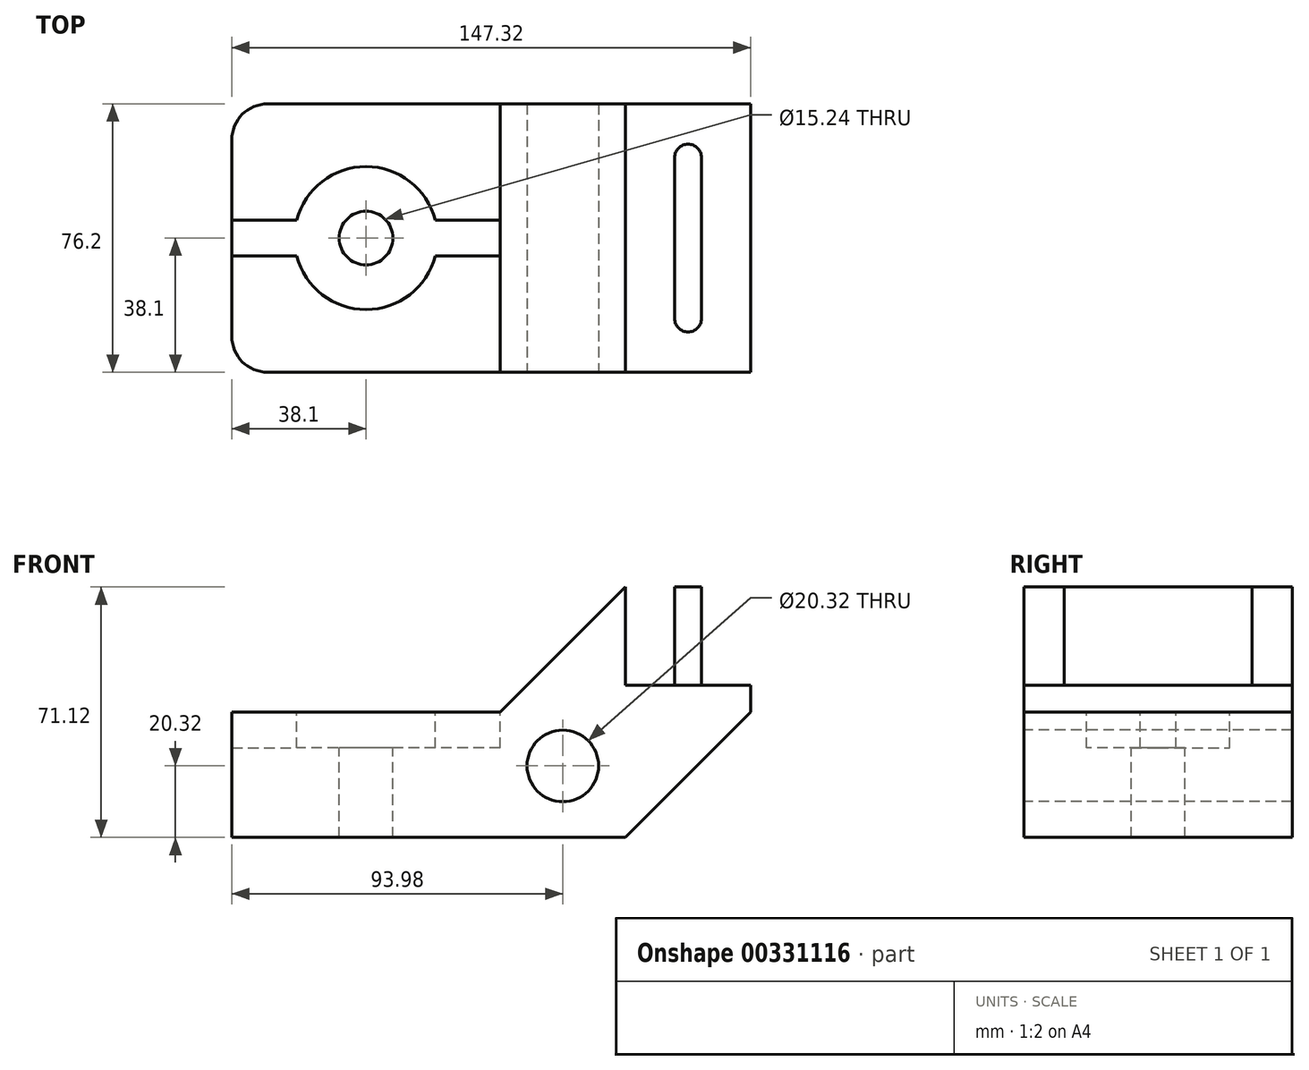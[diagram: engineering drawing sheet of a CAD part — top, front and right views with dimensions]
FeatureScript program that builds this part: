
annotation { "Feature Type Name" : "Feature", "Feature Type Description" : "" }
export const myFeature = defineFeature(function(context is Context, id is Id, definition is map)
    precondition{}
    {
        {
            var Q0;
            Q0=qCreatedBy(makeId("Front.planeOp"),FACE);
            var sketch = newSketch(context, id + "F0", { "sketchPlane" : qUnion([Q0])});
            skLineSegment(sketch, "E0", {"start": v(0, 0) * mm, "end": v(0, 35.56) * mm});
            skLineSegment(sketch, "E1", {"start": v(0, 35.56) * mm, "end": v(76.2, 35.56) * mm});
            skLineSegment(sketch, "E2", {"start": v(76.2, 35.56) * mm, "end": v(111.76, 71.12) * mm});
            skLineSegment(sketch, "E3", {"start": v(111.76, 71.12) * mm, "end": v(147.32, 71.12) * mm});
            skLineSegment(sketch, "E4", {"start": v(147.32, 71.12) * mm, "end": v(147.32, 35.56) * mm});
            skLineSegment(sketch, "E5", {"start": v(147.32, 35.56) * mm, "end": v(111.76, 0) * mm});
            skLineSegment(sketch, "E6", {"start": v(111.76, 0) * mm, "end": v(0, 0) * mm});
            skSolve(sketch);
        }
        {
            var Q0;
            Q0=makeQuery(id+"F0.imprint","IMPRINT",FACE,{"disambiguationData":[TD([[makeQuery(id+"F0.imprint","IMPRINT",EDGE,{"derivedFrom":sQuery(id+"F0.wireOp",EDGE,"E0")}),-1.0]])]});
            extrude(context, id + "F1", {"entities" : qUnion([Q0]), "oppositeDirection" : true, "depth" : 76.2 * mm});
        }
        {
            var Q0;
            Q0=makeQuery(id+"F1.opExtrude","SWEPT_FACE",FACE,{"disambiguationData":[OSD([sQuery(id+"F0.wireOp",EDGE,"E3")])]});
            var sketch = newSketch(context, id + "F2", { "sketchPlane" : qUnion([Q0])});
            skLineSegment(sketch, "E7", {"start": v(129.54, 60.96) * mm, "end": v(129.54, 15.24) * mm, "construction": true});
            skArc(sketch, "E8.0.startCap", {"start": v(125.73, 60.96) * mm, "mid": v(129.54, 64.77) * mm, "end": v(133.35, 60.96) * mm});
            skArc(sketch, "E8.0.endCap", {"start": v(133.35, 15.24) * mm, "mid": v(129.54, 11.43) * mm, "end": v(125.73, 15.24) * mm});
            skLineSegment(sketch, "E8.0.left", {"start": v(133.35, 60.96) * mm, "end": v(133.35, 15.24) * mm});
            skLineSegment(sketch, "E8.0.right", {"start": v(125.73, 60.96) * mm, "end": v(125.73, 15.24) * mm});
            skSolve(sketch);
        }
        {
            var Q0;
            Q0=makeQuery(id+"F2.imprint","IMPRINT",FACE,{"disambiguationData":[TD([[makeQuery(id+"F2.imprint","IMPRINT",EDGE,{"derivedFrom":sQuery(id+"F2.wireOp",EDGE,"E8.0.startCap")}),-1.0]])]});
            extrude(context, id + "F3", {"entities" : qUnion([Q0]), "operationType" : NewBodyOperationType.REMOVE, "oppositeDirection" : true, "depth" : 27.94 * mm});
        }
        {
            var Q0;
            Q0=makeQuery(id+"F1.opExtrude","SWEPT_FACE",FACE,{"disambiguationData":[OSD([sQuery(id+"F0.wireOp",EDGE,"E1")])]});
            var sketch = newSketch(context, id + "F4", { "sketchPlane" : qUnion([Q0])});
            skLineSegment(sketch, "E9", {"start": v(0, 43.18) * mm, "end": v(19.74, 43.18) * mm});
            skLineSegment(sketch, "E10", {"start": v(56.46, 43.18) * mm, "end": v(76.2, 43.18) * mm});
            skLineSegment(sketch, "E11", {"start": v(76.2, 43.18) * mm, "end": v(76.2, 33.02) * mm});
            skLineSegment(sketch, "E12", {"start": v(76.2, 33.02) * mm, "end": v(56.46, 33.02) * mm});
            skLineSegment(sketch, "E13", {"start": v(19.74, 33.02) * mm, "end": v(0, 33.02) * mm});
            skLineSegment(sketch, "E14", {"start": v(0, 33.02) * mm, "end": v(0, 43.18) * mm});
            skCircle(sketch, "E15", {"center": v(38.1, 38.1) * mm, "radius": 19.05 * mm});
            skSolve(sketch);
        }
        {
            var Q0;
            Q0=sQuery(id+"F4.wireOp",VERTEX,"E15.center");
            var Q1;
            Q1=makeQuery(id+"F1.opExtrude","SWEPT_BODY",BODY,{"disambiguationData":[OSD([sQuery(id+"F0.wireOp",EDGE,"E0"),sQuery(id+"F0.wireOp",EDGE,"E1"),sQuery(id+"F0.wireOp",EDGE,"E2"),sQuery(id+"F0.wireOp",EDGE,"E3"),sQuery(id+"F0.wireOp",EDGE,"E4"),sQuery(id+"F0.wireOp",EDGE,"E5"),sQuery(id+"F0.wireOp",EDGE,"E6")])]});
            hole(context, id + "F5", {"style" : HoleStyle.C_BORE, "endStyle" : HoleEndStyle.THROUGH, "holeDiameter" : 15.24 * mm, "cBoreDiameter" : 40.64 * mm, "cBoreDepth" : 10.16 * mm, "tappedDepth" : 12.7 * mm, "tapClearance" : 3, "locations" : qUnion([Q0]), "scope" : qUnion([Q1])});
        }
        {
            var Q0;
            {var subQ0=sQuery(id+"F4.wireOp",EDGE,"E9");Q0=makeQuery(id+"F4.imprint","IMPRINT",FACE,{"disambiguationData":[TD([[makeQuery(id+"F4.imprint","IMPRINT",EDGE,{"derivedFrom":subQ0}),-1.0]])]});}
            var Q1;
            {var subQ0=sQuery(id+"F4.wireOp",EDGE,"E10");Q1=makeQuery(id+"F4.imprint","IMPRINT",FACE,{"disambiguationData":[TD([[makeQuery(id+"F4.imprint","IMPRINT",EDGE,{"derivedFrom":subQ0}),-1.0]])]});}
            extrude(context, id + "F6", {"entities" : qUnion([Q0, Q1]), "operationType" : NewBodyOperationType.REMOVE, "oppositeDirection" : true, "depth" : 10.16 * mm});
        }
        {
            var Q0;
            Q0=makeQuery(id+"F1.opExtrude","CAP_FACE",FACE,{"disambiguationData":[OSD([sQuery(id+"F0.wireOp",EDGE,"E0"),sQuery(id+"F0.wireOp",EDGE,"E1"),sQuery(id+"F0.wireOp",EDGE,"E2"),sQuery(id+"F0.wireOp",EDGE,"E3"),sQuery(id+"F0.wireOp",EDGE,"E4"),sQuery(id+"F0.wireOp",EDGE,"E5"),sQuery(id+"F0.wireOp",EDGE,"E6")])],"isStart":true});
            var sketch = newSketch(context, id + "F7", { "sketchPlane" : qUnion([Q0])});
            skCircle(sketch, "E16", {"center": v(93.98, 20.32) * mm, "radius": 10.16 * mm});
            skSolve(sketch);
        }
        {
            var Q0;
            Q0=makeQuery(id+"F7.imprint","IMPRINT",FACE,{"disambiguationData":[TD([[makeQuery(id+"F7.imprint","IMPRINT",EDGE,{"derivedFrom":sQuery(id+"F7.wireOp",EDGE,"E16")}),1.0]])]});
            extrude(context, id + "F8", {"entities" : qUnion([Q0]), "operationType" : NewBodyOperationType.REMOVE, "endBound" : BoundingType.THROUGH_ALL, "oppositeDirection" : true, "depth" : 25.4 * mm});
        }
        {
            var Q0;
            Q0=makeQuery(id+"F1.opExtrude","CAP_EDGE",EDGE,{"disambiguationData":[OSD([sQuery(id+"F0.wireOp",EDGE,"E0")])],"isStart":true});
            var Q1;
            Q1=makeQuery(id+"F1.opExtrude","CAP_EDGE",EDGE,{"disambiguationData":[OSD([sQuery(id+"F0.wireOp",EDGE,"E0")])],"isStart":false});
            fillet(context, id + "F9", {"entities" : qUnion([Q0, Q1]), "radius" : 10.16 * mm, "tangentPropagation" : true, "allowEdgeOverflow" : false});
        }
    });
